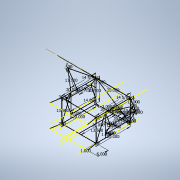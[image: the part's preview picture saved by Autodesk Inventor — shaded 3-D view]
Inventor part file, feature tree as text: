
AUTODESK INVENTOR PART (.ipt)
format: ipt  version: 2021 (Build 250183000, 183)  size: 210,944 bytes
history: native  units: in
note: dims shown in document units (in); Inventor stores cm internally (conversion verified against a paired STEP export)
features: sketch x17, plane x17, other x1
ambient origin geometry x8: Origin, YZ Plane, XZ Plane, XY Plane, X Axis, Y Axis, Z Axis, Center Point
feature tree (35):
  sketch  "Sketch1"  dims[d0=22.0in d1=6.75in d2=26.5in d3=20.0in d4=35.0in d5=38.0in d6=13.5in d7=13.5in d8=13.0in d9=22.0in]
  plane  "Work Plane2"
  sketch  "Sketch5"  dims[d11=10.0in]
  plane  "Work Plane1"
  sketch  "Sketch3"  dims[d10=11.0in]
  plane  "Work Plane3"
  sketch  "Sketch6"  dims[d12=20.0in]
  plane  "Work Plane4"
  sketch  "Sketch7"  dims[d16=14.625in]
  plane  "Work Plane5"
  sketch  "Sketch8"  dims[d17=2.0in]
  plane  "Work Plane7"
  sketch  "Sketch9"  dims[d18=-6.5in]
  plane  "Work Plane8"
  sketch  "Sketch10"  dims[d19=6.0in]
  plane  "Work Plane9"
  sketch  "Sketch11"  dims[d20=1.0in]
  plane  "Work Plane10"
  sketch  "Sketch13"  dims[d21=20.0in]
  plane  "Work Plane11"
  sketch  "Sketch14"  dims[d22=13.0in d25=-26.0in]
  plane  "Work Plane12"
  sketch  "Sketch15"  dims[d26=20.0in]
  plane  "Work Plane13"
  sketch  "Sketch16"  dims[d29=13.5in]
  plane  "Work Plane15"
  sketch  "Sketch17"  dims[d30=20.0in]
  plane  "Work Plane16"
  sketch  "Sketch18"  dims[d31=13.0in]
  plane  "Work Plane17"
  sketch  "Sketch19"  dims[d32=14.625in]
  plane  "Work Plane18"
  sketch  "Sketch20"  dims[d33=0.5in d34=13.5in d35=13.5in d36=-10.0in d37=20.0in d38=14.625in d39=2.0in d40=20.0in d41=13.5in d42=13.0in d43=14.625in d44=0.5in d47=8.0in d48=3.0in d49=3.0in d50=2.0in d51=2.0in d52=1.25in d53=1.25in d54=15.625in d55=0.5in d56=2.0in d58=2.0in d59=1.25in d60=2.0in d61=1.25in d62=0.8532in d63=11.5in d65=0.5in d66=-0.8532in d67=11.5in d68=7.3125in d69=0.5in d70=20.5in d74=20.0in d75=3.0in d76=3.0in d77=3.0in d78=5.0in d79=8.0in d80=1.5in d81=7.8125in d82=20.5in d83=0.75in d84=0.75in]
  other  "Work Axis1"
  plane  "Work Plane14"
